# Revit family: Pipefitting_IBP_Conex_MaxiPro_FittingReducer_MP5243
name_source: partatom
category: Pipe Fittings
units: mm (PartAtom-declared; Revit-internal decimal feet)

## family parameters
Always vertical = No
Cut with Voids When Loaded = No
OmniClass Number = 23.65.00.00
OmniClass Title = Supply and Distribution of Liquids and Gases
Part Type = Transition
Round Connector Dimension = Use Diameter
Shared = No
Work Plane-Based = No

## types (13) — shared parameters
Angle = 30.00°
Application = Air conditioning & refrigeration
Assembly Code = D20
AssetType = Fixed
BIMObjectName = PipefittingP_IBP_Conex_MaxiPro_FittingReducer_MP5243
ClassificationName = Uniclass2015
ClassificationValue = Pr_65_52_63_18
Description = Fitting Reducer
ExpectedServiceLifeYears = 25
FittingType = Fitting Reducer
FluidTemperatureMax = 121 °C
FluidTemperatureMin = -40 °C
IfcExportAs = IfcPipeFitting
IfcExportType = IfcPipeFittingType
Keynote = S
Manufacturer = Conex Banninger
ManufacturerName = IBP
Material = Copper, C12200
MaterialType = Refrigerant Grade Copper, C12200
MaxHydrostaticPressure = 48 bar
NBSDescription = Copper pipeline fittings
NBSObjectName = IBP - Copper pipeline fittings
NBSReference = 90-10-65/315
ORingTemperatureRange = -40°C to 140°C
PipeConnectorType = Press x Male Copper
PressJawCompatability = MaxiPro Jaws supplied by Rothenberger
SealType = HNBR
Shape = Cylindrical
SurfaceFinish = Natural
URL = http://www.conexbanninger.com
WarrantyDescription = Product Guarantee
WarrantyDurationMonths = 60
Weight = 0.00 kg
_BimstoreBibleVersion = 14
_CurrentRevision = 1
_DistributedBy = www.bimmepaus.com.au/
zero-valued in all types: NominalDepth, NominalHeight, NominalLength, _BimSpecGuid

## per-type parameters (varying)
| type | A_OverallLength | B | BeadDepth | BeadLocation_Formula | Bead_Dia | C | Length | Model | ModelNumber | ModelReference | OD_PlainTail | PlainTail_ID_Formula | PressEndOD_formula | ProductCode | S | Size | TubeStopLocation_Formula | Type Comments | d1_PressEndID |
| MP5243 0030200 1/4" x 3/8" male copper | 44 mm | 5 mm  [stored 0.0164042 ft] | 8 mm  [stored 0.0262467 ft] | 37 mm | 2 mm  [stored 0.00656168 ft] | 21 mm  [stored 0.0688976 ft] | 44 mm | MP5243 0030200 | MP5243 0030200 | 1/4" x 3/8" male copper | 10 mm  [stored 0.0328084 ft] | 7 mm  [stored 0.0229659 ft] | 9 mm  [stored 0.0295276 ft] | MP5243 0030200 | 1 mm  [stored 0.00328084 ft] | 1/4" x 3/8" male copper | 26 mm | 1/4" x 3/8" male copper | 6 mm  [stored 0.019685 ft] |
| MP5243 0040300 3/8" x 1/2" male copper | 45 mm | 7 mm  [stored 0.0229659 ft] | 7 mm  [stored 0.0229659 ft] | 38 mm | 2 mm  [stored 0.00656168 ft] | 21 mm  [stored 0.0688976 ft] | 45 mm | MP5243 0040300 | MP5243 0040300 | 3/8" x 1/2" male copper | 13 mm | 10 mm  [stored 0.0328084 ft] | 12 mm  [stored 0.0393701 ft] | MP5243 0040300 | 1 mm  [stored 0.00328084 ft] | 3/8" x 1/2" male copper | 27 mm | 3/8" x 1/2" male copper | 10 mm  [stored 0.0328084 ft] |
| MP5243 0050300 3/8" x 5/8" male copper | 47 mm | 6 mm  [stored 0.019685 ft] | 7 mm  [stored 0.0229659 ft] | 40 mm | 2 mm  [stored 0.00656168 ft] | 24 mm | 47 mm | MP5243 0050300 | MP5243 0050300 | 3/8" x 5/8" male copper | 16 mm | 14 mm  [stored 0.0459318 ft] | 12 mm  [stored 0.0393701 ft] | MP5243 0050300 | 1 mm  [stored 0.00328084 ft] | 3/8" x 5/8" male copper | 30 mm | 3/8" x 5/8" male copper | 10 mm  [stored 0.0328084 ft] |
| MP5243 0050400 1/2" x 5/8" male copper | 46 mm | 5 mm  [stored 0.0164042 ft] | 7 mm  [stored 0.0229659 ft] | 39 mm | 3 mm  [stored 0.00984252 ft] | 24 mm | 46 mm | MP5243 0050400 | MP5243 0050400 | 1/2" x 5/8" male copper | 16 mm | 14 mm  [stored 0.0459318 ft] | 15 mm  [stored 0.0492126 ft] | MP5243 0050400 | 1 mm  [stored 0.00328084 ft] | 1/2" x 5/8" male copper | 29 mm | 1/2" x 5/8" male copper | 13 mm |
| MP5243 0060400 1/2" x 3/4" male copper | 53 mm | 11 mm | 7 mm  [stored 0.0229659 ft] | 46 mm | 3 mm  [stored 0.00984252 ft] | 25 mm  [stored 0.082021 ft] | 53 mm | MP5243 0060400 | MP5243 0060400 | 1/2" x 3/4" male copper | 19 mm | 17 mm | 15 mm  [stored 0.0492126 ft] | MP5243 0060400 | 1 mm  [stored 0.00328084 ft] | 1/2" x 3/4" male copper | 36 mm | 1/2" x 3/4" male copper | 13 mm |
| MP5243 0060500 5/8" x 3/4" male copper | 53 mm | 8 mm  [stored 0.0262467 ft] | 8 mm  [stored 0.0262467 ft] | 45 mm | 3 mm  [stored 0.00984252 ft] | 25 mm  [stored 0.082021 ft] | 53 mm | MP5243 0060500 | MP5243 0060500 | 5/8" x 3/4" male copper | 19 mm | 17 mm | 18 mm | MP5243 0060500 | 1 mm  [stored 0.00328084 ft] | 5/8" x 3/4" male copper | 33 mm | 5/8" x 3/4" male copper | 16 mm |
| MP5243 0070400 1/2" x 7/8" male copper | 54 mm | 10 mm  [stored 0.0328084 ft] | 8 mm  [stored 0.0262467 ft] | 46 mm | 3 mm  [stored 0.00984252 ft] | 25 mm  [stored 0.082021 ft] | 54 mm | MP5243 0070400 | MP5243 0070400 | 1/2" x 7/8" male copper | 22 mm | 20 mm | 15 mm  [stored 0.0492126 ft] | MP5243 0070400 | 1 mm  [stored 0.00328084 ft] | 1/2" x 7/8" male copper | 35 mm | 1/2" x 7/8" male copper | 13 mm |
| MP5243 0070500 5/8" x 7/8" male copper | 55 mm | 7 mm  [stored 0.0229659 ft] | 8 mm  [stored 0.0262467 ft] | 47 mm | 3 mm  [stored 0.00984252 ft] | 27 mm | 55 mm | MP5243 0070500 | MP5243 0070500 | 5/8" x 7/8" male copper | 22 mm | 19 mm | 19 mm | MP5243 0070500 | 2 mm  [stored 0.00656168 ft] | 5/8" x 7/8" male copper | 34 mm | 5/8" x 7/8" male copper | 16 mm |
| MP5243 0070600 3/4" x 7/8" male copper | 53 mm | 4 mm  [stored 0.0131234 ft] | 8 mm  [stored 0.0262467 ft] | 45 mm | 3 mm  [stored 0.00984252 ft] | 27 mm | 53 mm | MP5243 0070600 | MP5243 0070600 | 3/4" x 7/8" male copper | 22 mm | 20 mm | 22 mm | MP5243 0070600 | 1 mm  [stored 0.00328084 ft] | 3/4" x 7/8" male copper | 31 mm | 3/4" x 7/8" male copper | 19 mm |
| MP5243 0090400 1/2" x 1 1/8" male copper | 61 mm | 15 mm  [stored 0.0492126 ft] | 7 mm  [stored 0.0229659 ft] | 54 mm | 3 mm  [stored 0.00984252 ft] | 29 mm | 61 mm | MP5243 0090400 | MP5243 0090400 | 1/2" x 1 1/8" male copper | 29 mm | 25 mm  [stored 0.082021 ft] | 16 mm | MP5243 0090400 | 2 mm  [stored 0.00656168 ft] | 1/2" x 1 1/8" male copper | 44 mm | 1/2" x 1 1/8" male copper | 13 mm |
| MP5243 0090500 5/8" x 1 1/8" male copper | 61 mm | 12 mm  [stored 0.0393701 ft] | 7 mm  [stored 0.0229659 ft] | 54 mm | 3 mm  [stored 0.00984252 ft] | 29 mm | 61 mm | MP5243 0090400 | MP5243 0090400 | 1/2" x 1 1/8" male copper | 29 mm | 25 mm  [stored 0.082021 ft] | 20 mm | MP5243 0090400 | 2 mm  [stored 0.00656168 ft] | 1/2" x 1 1/8" male copper | 41 mm | 1/2" x 1 1/8" male copper | 16 mm |
| MP5243 0090600 3/4" x 1 1/8" male copper | 60 mm | 10 mm  [stored 0.0328084 ft] | 10 mm  [stored 0.0328084 ft] | 50 mm | 3 mm  [stored 0.00984252 ft] | 29 mm | 60 mm | MP5243 0090600 | MP5243 0090600 | 3/4" x 1 1/8" male copper | 29 mm | 25 mm  [stored 0.082021 ft] | 23 mm | MP5243 0090600 | 2 mm  [stored 0.00656168 ft] | 3/4" x 1 1/8" male copper | 38 mm | 3/4" x 1 1/8" male copper | 19 mm |
| MP5243 0090700 7/8" x 1 1/8" male copper | 60 mm | 7 mm  [stored 0.0229659 ft] | 10 mm  [stored 0.0328084 ft] | 50 mm | 3 mm  [stored 0.00984252 ft] | 29 mm | 60 mm | MP5243 0090700 | MP5243 0090700 | 7/8" x 1 1/8" male copper | 29 mm | 25 mm  [stored 0.082021 ft] | 26 mm | MP5243 0090700 | 2 mm  [stored 0.00656168 ft] | 7/8" x 1 1/8" male copper | 36 mm | 7/8" x 1 1/8" male copper | 22 mm |

note: [stored X ft] marks values corroborated as IEEE doubles in the binary element streams (Revit-internal decimal feet)

## geometry (parser evidence)
native form markers: Sweep x7
no freeform markers — native parametric forms only
